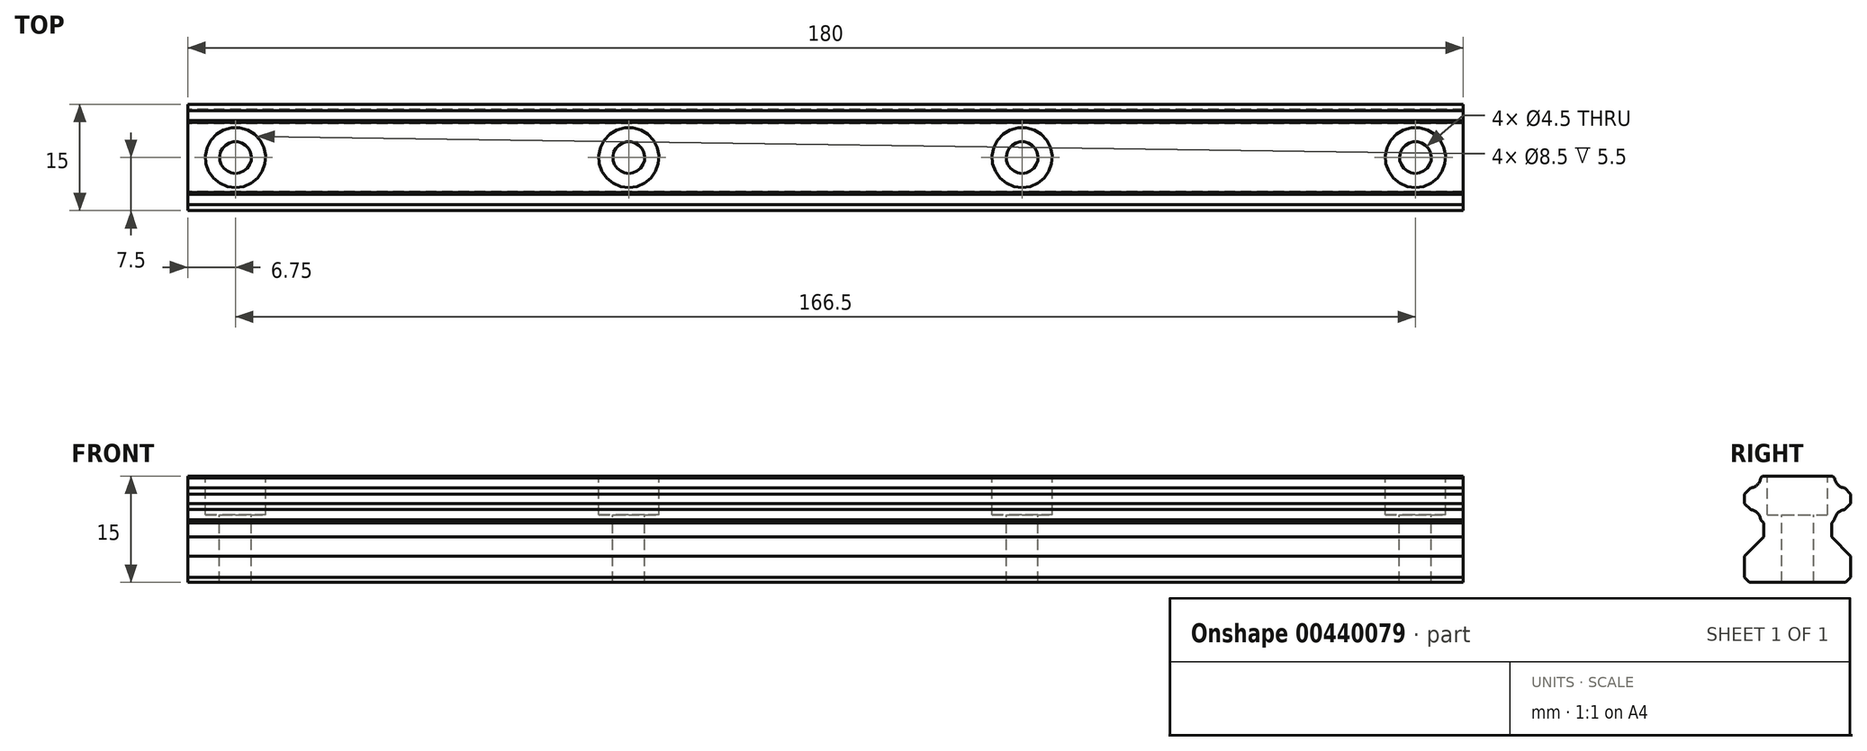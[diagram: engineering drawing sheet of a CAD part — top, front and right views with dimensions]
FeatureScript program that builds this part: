
annotation { "Feature Type Name" : "Feature", "Feature Type Description" : "" }
export const myFeature = defineFeature(function(context is Context, id is Id, definition is map)
    precondition{}
    {
        {
            var Q0;
            Q0=qCreatedBy(makeId("Right.planeOp"),FACE);
            var sketch = newSketch(context, id + "F0", { "sketchPlane" : qUnion([Q0])});
            skLineSegment(sketch, "E0.0.0", {"start": v(6.8, 0) * mm, "end": v(-6.8, 0) * mm});
            skLineSegment(sketch, "E0.0.1", {"start": v(-6.8, 0) * mm, "end": v(-7.5, 0.7) * mm});
            skLineSegment(sketch, "E0.0.2", {"start": v(-7.5, 0.7) * mm, "end": v(-7.5, 3.7) * mm});
            skLineSegment(sketch, "E0.0.3", {"start": v(-7.5, 3.7) * mm, "end": v(-4.8, 6.4) * mm});
            skLineSegment(sketch, "E0.0.4", {"start": v(-4.8, 6.4) * mm, "end": v(-4.8, 8.4) * mm});
            skLineSegment(sketch, "E0.0.5", {"start": v(-4.8, 8.4) * mm, "end": v(-5.2, 8.81) * mm});
            skArc(sketch, "E0.0.6", {"start": v(-5.2, 8.81) * mm, "mid": v(-5.67, 9.79) * mm, "end": v(-6.65, 10.26) * mm});
            skLineSegment(sketch, "E0.0.7", {"start": v(-6.65, 10.26) * mm, "end": v(-7.5, 11.1) * mm});
            skLineSegment(sketch, "E0.0.8", {"start": v(-7.5, 11.1) * mm, "end": v(-7.5, 12.45) * mm});
            skLineSegment(sketch, "E0.0.9", {"start": v(-7.5, 12.45) * mm, "end": v(-6.63, 13.31) * mm});
            skArc(sketch, "E0.0.10", {"start": v(-6.63, 13.31) * mm, "mid": v(-5.67, 13.78) * mm, "end": v(-5.2, 14.75) * mm});
            skLineSegment(sketch, "E0.0.11", {"start": v(-5.2, 14.75) * mm, "end": v(-4.95, 15) * mm});
            skLineSegment(sketch, "E0.0.12", {"start": v(-4.95, 15) * mm, "end": v(4.95, 15) * mm});
            skLineSegment(sketch, "E0.0.13", {"start": v(4.95, 15) * mm, "end": v(5.2, 14.75) * mm});
            skArc(sketch, "E0.0.14", {"start": v(5.2, 14.75) * mm, "mid": v(5.67, 13.78) * mm, "end": v(6.63, 13.31) * mm});
            skLineSegment(sketch, "E0.0.15", {"start": v(6.63, 13.31) * mm, "end": v(7.5, 12.45) * mm});
            skLineSegment(sketch, "E0.0.16", {"start": v(7.5, 12.45) * mm, "end": v(7.5, 11.1) * mm});
            skLineSegment(sketch, "E0.0.17", {"start": v(7.5, 11.1) * mm, "end": v(6.65, 10.26) * mm});
            skArc(sketch, "E0.0.18", {"start": v(6.65, 10.26) * mm, "mid": v(5.67, 9.79) * mm, "end": v(5.2, 8.81) * mm});
            skLineSegment(sketch, "E0.0.19", {"start": v(5.2, 8.81) * mm, "end": v(4.8, 8.4) * mm});
            skLineSegment(sketch, "E0.0.20", {"start": v(4.8, 8.4) * mm, "end": v(4.8, 6.4) * mm});
            skLineSegment(sketch, "E0.0.21", {"start": v(4.8, 6.4) * mm, "end": v(7.5, 3.7) * mm});
            skLineSegment(sketch, "E0.0.22", {"start": v(7.5, 3.7) * mm, "end": v(7.5, 0.7) * mm});
            skLineSegment(sketch, "E0.0.23", {"start": v(7.5, 0.7) * mm, "end": v(6.8, 0) * mm});
            skSolve(sketch);
        }
        {
            var Q0;
            Q0=makeQuery(id+"F0.imprint","IMPRINT",FACE,{"disambiguationData":[TD([[makeQuery(id+"F0.imprint","IMPRINT",EDGE,{"derivedFrom":sQuery(id+"F0.wireOp",EDGE,"E0.0.0")}),-1.0]])]});
            extrude(context, id + "F1", {"entities" : qUnion([Q0]), "depth" : 180 * mm});
        }
        {
            var Q0;
            Q0=makeQuery(id+"F1.opExtrude","SWEPT_FACE",FACE,{"disambiguationData":[OSD([sQuery(id+"F0.wireOp",EDGE,"E0.0.12")])]});
            var sketch = newSketch(context, id + "F2", { "sketchPlane" : qUnion([Q0])});
            skLineSegment(sketch, "E1", {"start": v(0, 0) * mm, "end": v(180, 0) * mm, "construction": true});
            skPoint(sketch, "E2", {"position": v(6.75, 0) * mm});
            skPoint(sketch, "E3", {"position": v(62.25, 0) * mm});
            skPoint(sketch, "E4", {"position": v(117.75, 0) * mm});
            skPoint(sketch, "E5", {"position": v(173.25, 0) * mm});
            skSolve(sketch);
        }
        {
            var Q0;
            Q0=sQuery(id+"F2.wireOp",VERTEX,"E2");
            var Q1;
            Q1=sQuery(id+"F2.wireOp",VERTEX,"E3");
            var Q2;
            Q2=sQuery(id+"F2.wireOp",VERTEX,"E4");
            var Q3;
            Q3=sQuery(id+"F2.wireOp",VERTEX,"E5");
            var Q4;
            Q4=makeQuery(id+"F1.opExtrude","SWEPT_BODY",BODY,{"disambiguationData":[OSD([sQuery(id+"F0.wireOp",EDGE,"E0.0.0"),sQuery(id+"F0.wireOp",EDGE,"E0.0.1"),sQuery(id+"F0.wireOp",EDGE,"E0.0.2"),sQuery(id+"F0.wireOp",EDGE,"E0.0.3"),sQuery(id+"F0.wireOp",EDGE,"E0.0.4"),sQuery(id+"F0.wireOp",EDGE,"E0.0.5"),sQuery(id+"F0.wireOp",EDGE,"E0.0.6"),sQuery(id+"F0.wireOp",EDGE,"E0.0.7"),sQuery(id+"F0.wireOp",EDGE,"E0.0.8"),sQuery(id+"F0.wireOp",EDGE,"E0.0.9"),sQuery(id+"F0.wireOp",EDGE,"E0.0.10"),sQuery(id+"F0.wireOp",EDGE,"E0.0.11"),sQuery(id+"F0.wireOp",EDGE,"E0.0.12"),sQuery(id+"F0.wireOp",EDGE,"E0.0.13"),sQuery(id+"F0.wireOp",EDGE,"E0.0.14"),sQuery(id+"F0.wireOp",EDGE,"E0.0.15"),sQuery(id+"F0.wireOp",EDGE,"E0.0.16"),sQuery(id+"F0.wireOp",EDGE,"E0.0.17"),sQuery(id+"F0.wireOp",EDGE,"E0.0.18"),sQuery(id+"F0.wireOp",EDGE,"E0.0.19"),sQuery(id+"F0.wireOp",EDGE,"E0.0.20"),sQuery(id+"F0.wireOp",EDGE,"E0.0.21"),sQuery(id+"F0.wireOp",EDGE,"E0.0.22"),sQuery(id+"F0.wireOp",EDGE,"E0.0.23")])]});
            hole(context, id + "F3", {"style" : HoleStyle.C_BORE, "endStyle" : HoleEndStyle.THROUGH, "holeDiameter" : 4.5 * mm, "cBoreDiameter" : 8.5 * mm, "cBoreDepth" : 5.5 * mm, "isTappedThrough" : true, "tappedDepth" : 26.25 * mm, "tapClearance" : 3, "locations" : qUnion([Q0, Q1, Q2, Q3]), "scope" : qUnion([Q4])});
        }
    });
